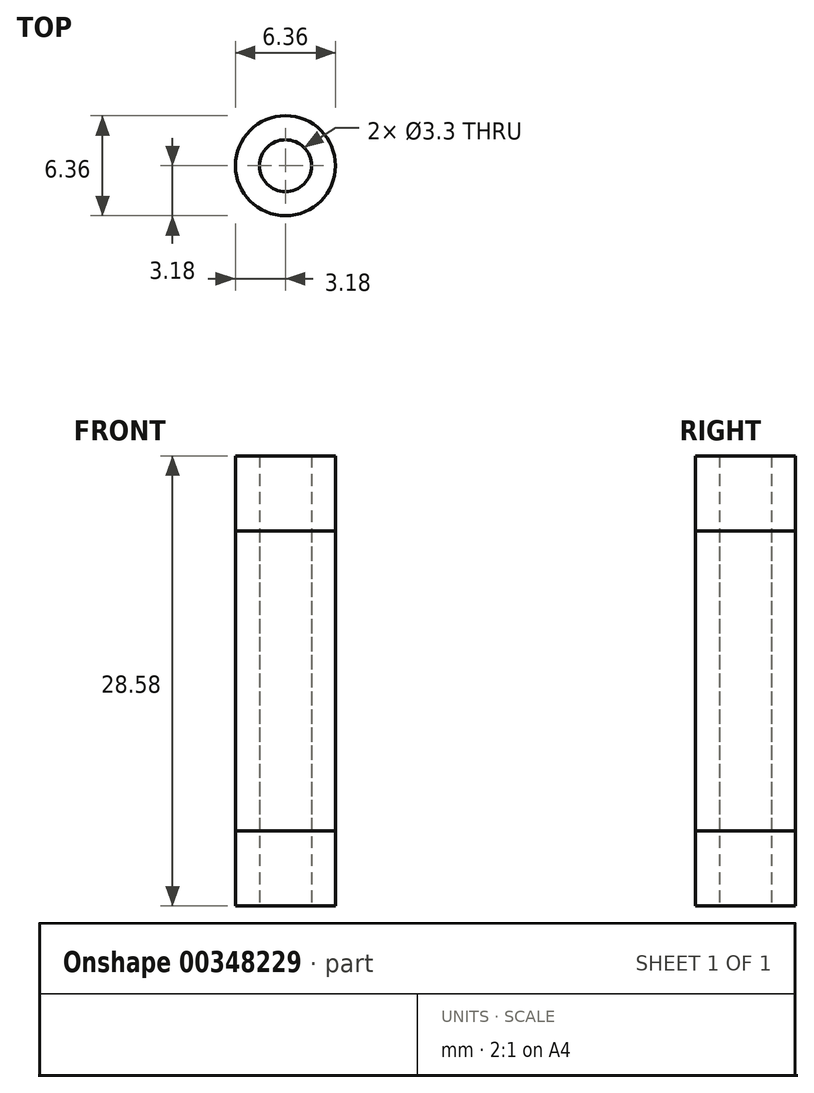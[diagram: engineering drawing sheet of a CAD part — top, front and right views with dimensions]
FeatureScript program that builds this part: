
annotation { "Feature Type Name" : "Feature", "Feature Type Description" : "" }
export const myFeature = defineFeature(function(context is Context, id is Id, definition is map)
    precondition{}
    {
        {
            var Q0;
            Q0=qCreatedBy(makeId("Top.planeOp"),FACE);
            var sketch = newSketch(context, id + "F0", { "sketchPlane" : qUnion([Q0])});
            skCircle(sketch, "E0", {"center": v(0, 0) * mm, "radius": 3.18 * mm});
            skCircle(sketch, "E1", {"center": v(0, 0) * mm, "radius": 1.65 * mm});
            skSolve(sketch);
        }
        {
            var Q0;
            Q0=qSketchRegion(id+"F0",true);
            extrude(context, id + "F1", {"entities" : qUnion([Q0]), "endBound" : BoundingType.SYMMETRIC, "depth" : 28.57 * mm});
        }
        {
            var Q0;
            Q0=qCreatedBy(makeId("Top.planeOp"),FACE);
            var sketch = newSketch(context, id + "F2", { "sketchPlane" : qUnion([Q0])});
            skCircle(sketch, "E2", {"center": v(0, 0) * mm, "radius": 3.18 * mm});
            skCircle(sketch, "E3", {"center": v(0, 0) * mm, "radius": 1.65 * mm});
            skSolve(sketch);
        }
        {
            var Q0;
            Q0=qSketchRegion(id+"F2",true);
            extrude(context, id + "F3", {"entities" : qUnion([Q0]), "endBound" : BoundingType.SYMMETRIC, "depth" : 19.05 * mm});
        }
    });
